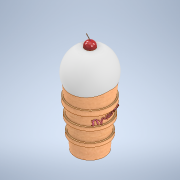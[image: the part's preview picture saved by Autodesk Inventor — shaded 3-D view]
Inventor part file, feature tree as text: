
AUTODESK INVENTOR PART (.ipt)
format: ipt  version: 2022 (Build 260153000, 153)  size: 506,368 bytes
history: native  units: mm
features: sketch x16, other x11, extrude x3, loft x2, revolve x2
ambient origin geometry x8: Origin, YZ Plane, XZ Plane, XY Plane, X Axis, Y Axis, Z Axis, Center Point
bodies: Body1 (feature_tree)
feature tree (34):
  other  "Твердое тело1"
  sketch  "Эскиз1"
  other  "РабПлоскость1"
  loft  "Лофт1"
  sketch  "Эскиз5"
  revolve  "Вращение1"
  other  "РабПлоскость7"
  sketch  "Эскиз7"
  sketch  "Эскиз8"
  sketch  "Эскиз9"
  extrude  "Выдавливание1"  Depth=50.0mm
  extrude  "Выдавливание2"  Depth=35.0mm
  other  "РабПлоскость8"
  sketch  "Эскиз12"
  revolve  "Вращение2"
  sketch  "Эскиз14"
  other  "РабПлоскость9"
  sketch  "Эскиз17"
  extrude  "Выдавливание4"  TaperAngle=0.0deg  [1 undecoded]
  sketch  "Эскиз21"
  other  "РабПлоскость12"
  other  "РабПлоскость13"
  other  "Рельеф1"
  other  "РабПлоскость14"
  loft  "Лофт4"
  sketch  "Эскиз3"
  sketch  "Эскиз6"
  other  "РабПлоскость5"
  other  "РабПлоскость6"
  sketch  "Эскиз10"
  sketch  "Эскиз13"
  sketch  "Эскиз19"
  sketch  "Эскиз23"
  sketch  "Эскиз24"
note: 1 required parameter value undecoded (feature->parameter linkage not recoverable at this tier; creation-order binding heuristic only, values carry confidence <= 0.55)
